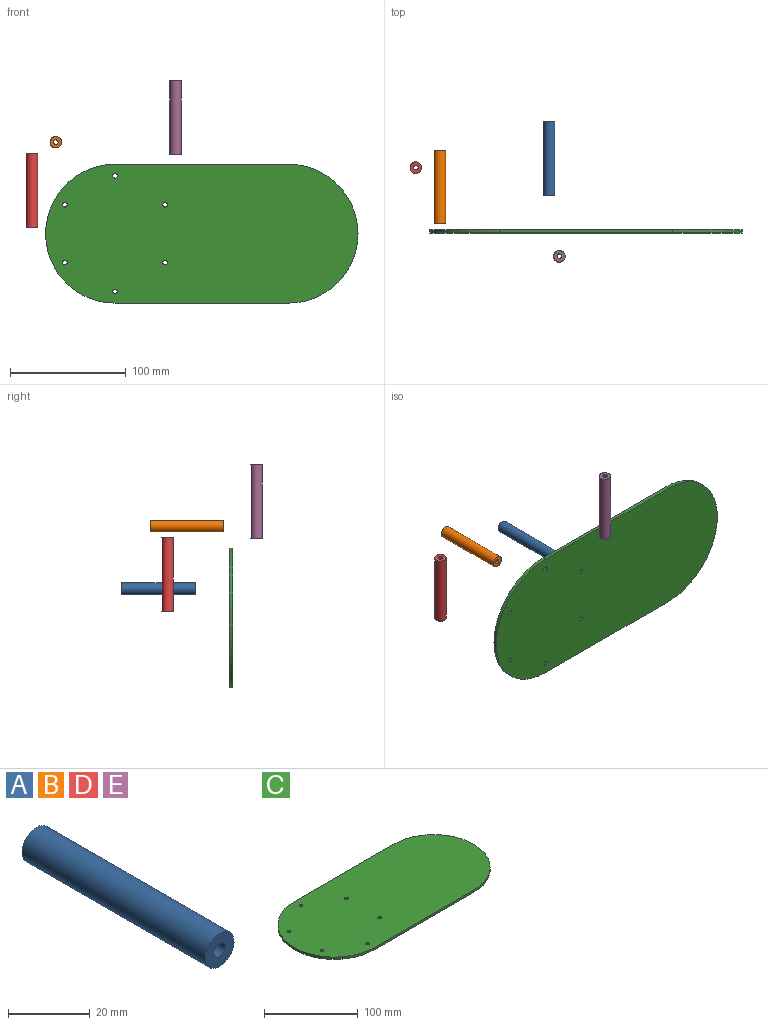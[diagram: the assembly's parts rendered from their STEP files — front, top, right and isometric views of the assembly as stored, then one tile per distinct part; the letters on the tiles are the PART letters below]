
ASSEMBLY  parts=5 mates=1
PART A: 4 faces, bbox 10x63.5x10 mm
  f0: plane 10x10mm, normal (0,1,0), area 66mm2, adj f2,f3
  f1: plane 10x10mm, normal (0,-1,0), area 66mm2, adj f2,f3
  f2: cylinder r=5mm len=63.5mm, axis (0,-1,0), area 1994.9mm2, adj f0,f1
  f3: cylinder r=2mm len=63.5mm, axis (0,-1,0), area 798mm2, adj f0,f1
PART B: same geometry as A
PART C: 12 faces, bbox 270x120x3 mm
  f0: plane 270x120mm, normal (0,0,1), area 29234.3mm2, adj f2,f3,f4,f5,f6,f7,f8,f9
  f1: plane 270x120mm, normal (0,0,-1), area 29234.3mm2, adj f2,f3,f4,f5,f6,f7,f8,f9
  f2: cylinder r=60mm len=120mm, axis (0,0,-1), area 565.5mm2, adj f0,f1,f3,f5
  f3: plane 150x3mm, normal (0,1,0), area 450mm2, adj f0,f1,f2,f4
  f4: cylinder r=60mm len=120mm, axis (0,0,-1), area 565.5mm2, adj f0,f1,f3,f5
  f5: plane 150x3mm, normal (0,-1,0), area 450mm2, adj f0,f1,f2,f4
  f6: cylinder r=2mm len=4mm, axis (0,0,-1), area 37.7mm2, adj f0,f1
  f7: cylinder r=2mm len=4mm, axis (0,0,-1), area 37.7mm2, adj f0,f1
  f8: cylinder r=2mm len=4mm, axis (0,0,-1), area 37.7mm2, adj f0,f1
  f9: cylinder r=2mm len=4mm, axis (0,0,-1), area 37.7mm2, adj f0,f1
  f10: cylinder r=2mm len=4mm, axis (0,0,-1), area 37.7mm2, adj f0,f1
  f11: cylinder r=2mm len=4mm, axis (0,0,-1), area 37.7mm2, adj f0,f1
PART D: same geometry as A
PART E: same geometry as A
PLACE A t=(48.74,95.02,-18.22)mm
PLACE B t=(-45.71,70.19,35.85)mm
PLACE C rot(axis=(1,0,0),90deg) t=(5.44,65.44,-43.22)mm
PLACE D rot(axis=(1,0,0),90deg) t=(-66.49,118.95,-37.61)mm
PLACE E rot(axis=(1,0,0),90deg) t=(57.61,42.15,25.35)mm
MATE slider C.f8 <-> A.f2  axis (0,1,0) through (48.74,65.44,-18.22)mm
